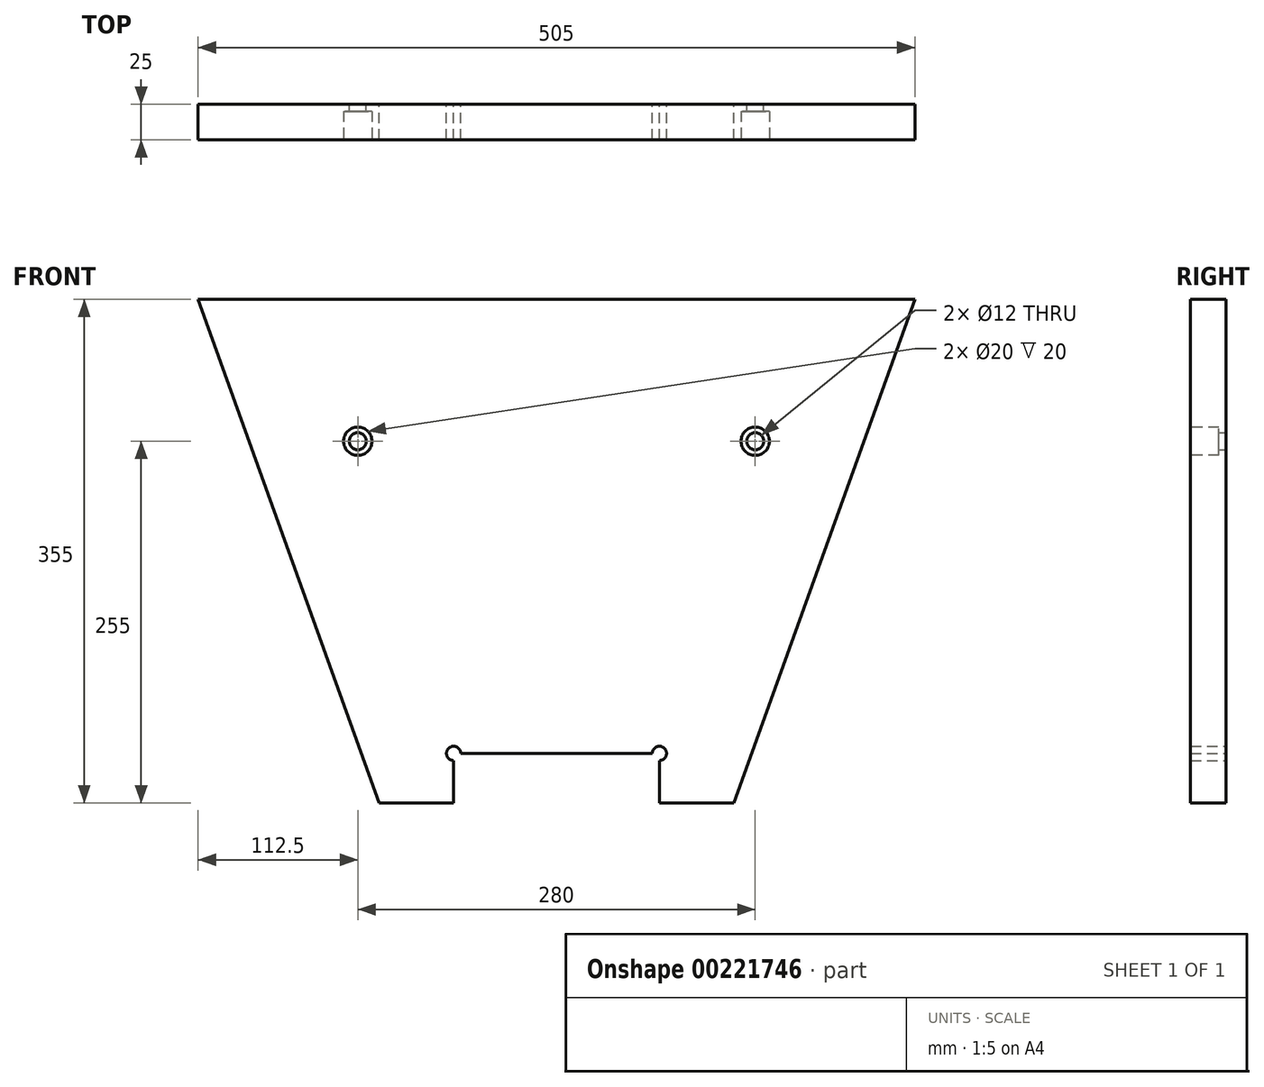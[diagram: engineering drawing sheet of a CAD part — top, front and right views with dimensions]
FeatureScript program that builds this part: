
annotation { "Feature Type Name" : "Feature", "Feature Type Description" : "" }
export const myFeature = defineFeature(function(context is Context, id is Id, definition is map)
    precondition{}
    {
        {
            var Q0;
            Q0=qCreatedBy(makeId("Front.planeOp"),FACE);
            var sketch = newSketch(context, id + "F0", { "sketchPlane" : qUnion([Q0])});
            skLineSegment(sketch, "E0", {"start": v(0, 0) * mm, "end": v(0, -355) * mm, "construction": true});
            skLineSegment(sketch, "E1", {"start": v(0, -355) * mm, "end": v(-125, -355) * mm});
            skLineSegment(sketch, "E2", {"start": v(-125, -355) * mm, "end": v(-252.5, 0) * mm});
            skLineSegment(sketch, "E3", {"start": v(-252.5, 0) * mm, "end": v(0, 0) * mm});
            skLineSegment(sketch, "E4.MirrorCS", {"start": v(252.5, 0) * mm, "end": v(0, 0) * mm});
            skLineSegment(sketch, "E5.MirrorCS", {"start": v(125, -355) * mm, "end": v(252.5, 0) * mm});
            skLineSegment(sketch, "E6.MirrorCS", {"start": v(0, -355) * mm, "end": v(125, -355) * mm});
            skCircle(sketch, "E7", {"center": v(-140, -100) * mm, "radius": 6 * mm});
            skCircle(sketch, "E8.MirrorC", {"center": v(140, -100) * mm, "radius": 6 * mm});
            skLineSegment(sketch, "E9.bottom", {"start": v(-72.5, -320) * mm, "end": v(72.5, -320) * mm});
            skLineSegment(sketch, "E9.top", {"start": v(-72.5, -390) * mm, "end": v(72.5, -390) * mm});
            skLineSegment(sketch, "E9.left", {"start": v(-72.5, -320) * mm, "end": v(-72.5, -390) * mm});
            skLineSegment(sketch, "E9.right", {"start": v(72.5, -320) * mm, "end": v(72.5, -390) * mm});
            skPoint(sketch, "E9.middle", {"position": v(0, -355) * mm});
            skCircle(sketch, "E10", {"center": v(-72.5, -320) * mm, "radius": 5 * mm});
            skCircle(sketch, "E11.MirrorC", {"center": v(72.5, -320) * mm, "radius": 5 * mm});
            skSolve(sketch);
        }
        {
            var Q0;
            {var subQ14=sQuery(id+"F0.wireOp",EDGE,"E2");Q0=makeQuery(id+"F0.imprint","IMPRINT",FACE,{"disambiguationData":[TD([[makeQuery(id+"F0.imprint","IMPRINT",EDGE,{"derivedFrom":subQ14}),-1.0]])]});}
            extrude(context, id + "F1", {"entities" : qUnion([Q0]), "depth" : 25 * mm});
        }
        {
            var Q0;
            Q0=makeQuery(id+"F1.opExtrude","CAP_FACE",FACE,{"disambiguationData":[OSD([sQuery(id+"F0.wireOp",EDGE,"E1"),sQuery(id+"F0.wireOp",EDGE,"E2"),sQuery(id+"F0.wireOp",EDGE,"E3"),sQuery(id+"F0.wireOp",EDGE,"E4.MirrorCS"),sQuery(id+"F0.wireOp",EDGE,"E5.MirrorCS"),sQuery(id+"F0.wireOp",EDGE,"E6.MirrorCS"),sQuery(id+"F0.wireOp",EDGE,"E7"),sQuery(id+"F0.wireOp",EDGE,"E8.MirrorC"),sQuery(id+"F0.wireOp",EDGE,"E9.bottom"),sQuery(id+"F0.wireOp",EDGE,"E9.left"),sQuery(id+"F0.wireOp",EDGE,"E9.right"),sQuery(id+"F0.wireOp",EDGE,"E10"),sQuery(id+"F0.wireOp",EDGE,"E11.MirrorC")])],"isStart":false});
            var sketch = newSketch(context, id + "F2", { "sketchPlane" : qUnion([Q0])});
            skCircle(sketch, "E12", {"center": v(-140, -100) * mm, "radius": 10 * mm});
            skCircle(sketch, "E13", {"center": v(140, -100) * mm, "radius": 10 * mm});
            skSolve(sketch);
        }
        {
            var Q0;
            Q0 = qSketchRegion(id + "F2", true);
            extrude(context, id + "F3", {"entities" : qUnion([Q0]), "operationType" : NewBodyOperationType.REMOVE, "oppositeDirection" : true, "depth" : 20 * mm});
        }
    });
